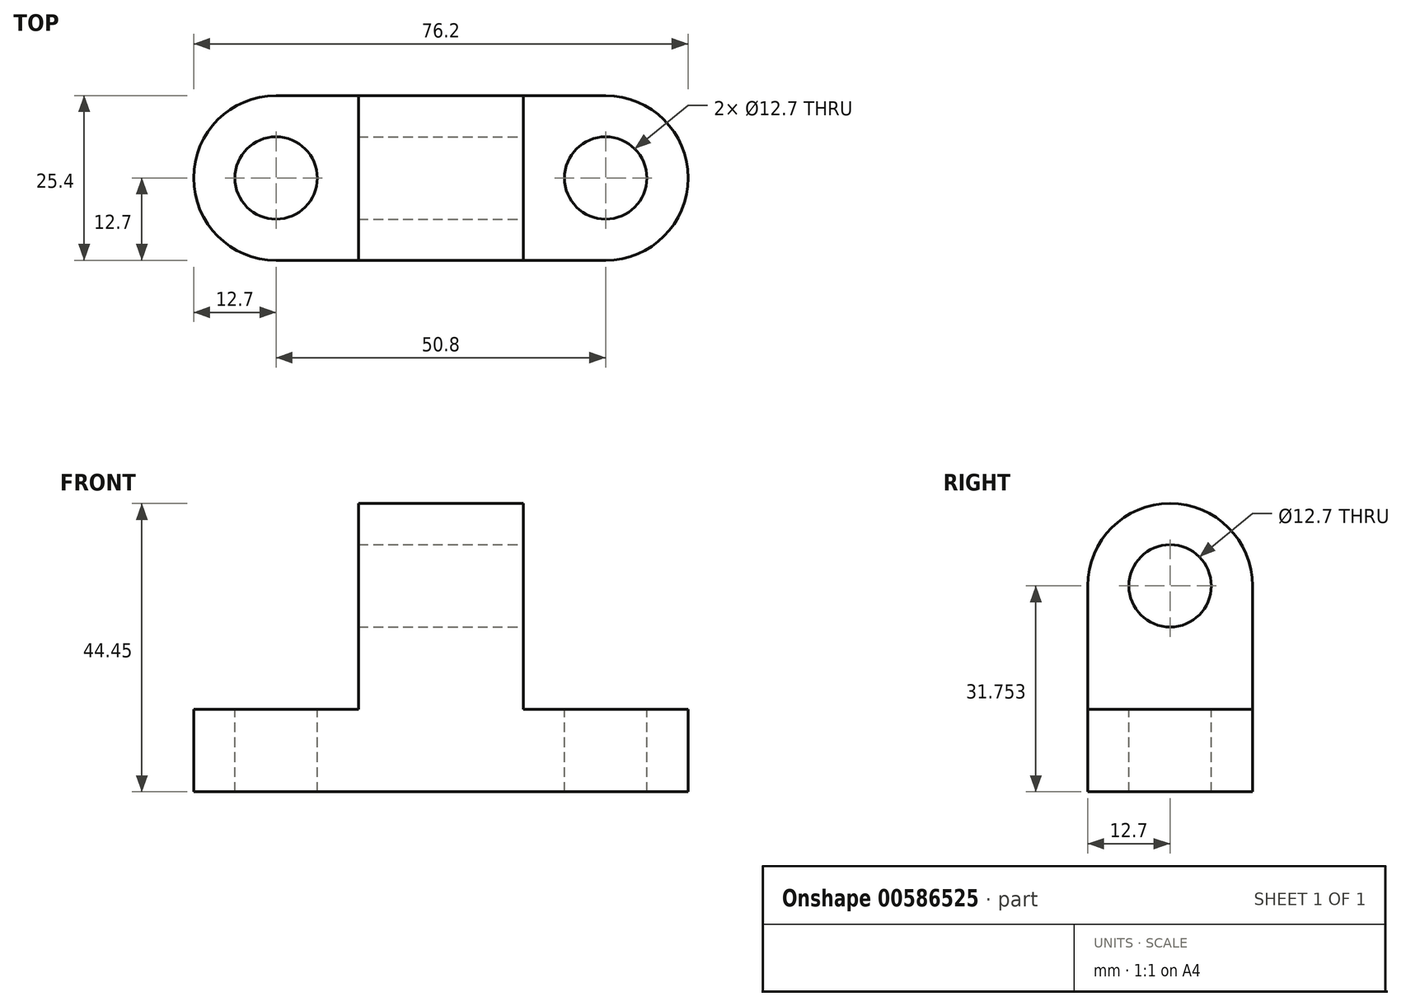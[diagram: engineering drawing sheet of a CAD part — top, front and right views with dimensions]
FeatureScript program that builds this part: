
annotation { "Feature Type Name" : "Feature", "Feature Type Description" : "" }
export const myFeature = defineFeature(function(context is Context, id is Id, definition is map)
    precondition{}
    {
        {
            var Q0;
            Q0=qCreatedBy(makeId("Front.planeOp"),FACE);
            var sketch = newSketch(context, id + "F0", { "sketchPlane" : qUnion([Q0])});
            skLineSegment(sketch, "E0", {"start": v(-85.26, 10.9) * mm, "end": v(-85.26, -1.8) * mm});
            skLineSegment(sketch, "E1", {"start": v(-85.26, -1.8) * mm, "end": v(-9.06, -1.8) * mm});
            skLineSegment(sketch, "E2", {"start": v(-9.06, -1.8) * mm, "end": v(-9.06, 10.9) * mm});
            skLineSegment(sketch, "E3", {"start": v(-9.06, 10.9) * mm, "end": v(-34.46, 10.9) * mm});
            skLineSegment(sketch, "E4", {"start": v(-34.46, 10.9) * mm, "end": v(-34.46, 42.65) * mm});
            skLineSegment(sketch, "E5", {"start": v(-34.46, 42.65) * mm, "end": v(-59.86, 42.65) * mm});
            skLineSegment(sketch, "E6", {"start": v(-59.86, 42.65) * mm, "end": v(-59.86, 10.9) * mm});
            skLineSegment(sketch, "E7", {"start": v(-59.86, 10.9) * mm, "end": v(-85.26, 10.9) * mm});
            skSolve(sketch);
        }
        {
            var Q0;
            Q0 = qSketchRegion(id + "F0", true);
            extrude(context, id + "F1", {"entities" : qUnion([Q0]), "depth" : 25.4 * mm, "offsetDistance" : 25.4 * mm});
        }
        {
            var Q0;
            Q0=makeQuery(id+"F1.opExtrude","SWEPT_FACE",FACE,{"disambiguationData":[OSD([sQuery(id+"F0.wireOp",EDGE,"E4")])]});
            var sketch = newSketch(context, id + "F2", { "sketchPlane" : qUnion([Q0])});
            skArc(sketch, "E8", {"start": v(0, 29.95) * mm, "mid": v(-12.7, 42.65) * mm, "end": v(-25.4, 29.95) * mm});
            skCircle(sketch, "E9", {"center": v(-12.7, 29.95) * mm, "radius": 6.35 * mm});
            skSolve(sketch);
        }
        {
            var Q0;
            Q0 = qSketchRegion(id + "F2", true);
            var Q1;
            {var subQ0=sQuery(id+"F2.wireOp",EDGE,"E8");var subQ1=sQuery(id+"F0.wireOp",EDGE,"E4");var subQ2=makeQuery(id+"F1.opExtrude","CAP_EDGE",EDGE,{"disambiguationData":[OSD([subQ1])],"isStart":true});var subQ3=makeQuery(id+"F2.imprint","INTERSECT",VERTEX,{"derivedFrom":[subQ2,subQ0]});Q1=makeQuery(id+"F2.imprint","IMPRINT",FACE,{"disambiguationData":[TD([[makeQuery(id+"F2.imprint","IMPRINT",EDGE,{"disambiguationData":[TD([[subQ3,-1.0]])],"derivedFrom":subQ0}),-1.0]])]});}
            var Q2;
            {var subQ0=sQuery(id+"F2.wireOp",EDGE,"E8");var subQ1=sQuery(id+"F0.wireOp",EDGE,"E4");var subQ2=makeQuery(id+"F1.opExtrude","CAP_EDGE",EDGE,{"disambiguationData":[OSD([subQ1])],"isStart":false});var subQ3=makeQuery(id+"F2.imprint","INTERSECT",VERTEX,{"derivedFrom":[subQ2,subQ0]});Q2=makeQuery(id+"F2.imprint","IMPRINT",FACE,{"disambiguationData":[TD([[makeQuery(id+"F2.imprint","IMPRINT",EDGE,{"disambiguationData":[TD([[subQ3,1.0]])],"derivedFrom":subQ0}),-1.0]])]});}
            extrude(context, id + "F3", {"entities" : qUnion([Q0, Q1, Q2]), "operationType" : NewBodyOperationType.REMOVE, "oppositeDirection" : true, "depth" : 25.4 * mm, "offsetDistance" : 25.4 * mm});
        }
        {
            var Q0;
            Q0=makeQuery(id+"F1.opExtrude","SWEPT_FACE",FACE,{"disambiguationData":[OSD([sQuery(id+"F0.wireOp",EDGE,"E3")])]});
            var sketch = newSketch(context, id + "F4", { "sketchPlane" : qUnion([Q0])});
            skArc(sketch, "E10", {"start": v(-21.76, -25.4) * mm, "mid": v(-9.06, -12.7) * mm, "end": v(-21.76, 0) * mm});
            skCircle(sketch, "E11", {"center": v(-21.76, -12.7) * mm, "radius": 6.35 * mm});
            skSolve(sketch);
        }
        {
            var Q0;
            Q0 = qSketchRegion(id + "F4", true);
            var Q1;
            {var subQ0=sQuery(id+"F4.wireOp",EDGE,"E10");var subQ1=sQuery(id+"F0.wireOp",EDGE,"E3");var subQ2=makeQuery(id+"F1.opExtrude","CAP_EDGE",EDGE,{"disambiguationData":[OSD([subQ1])],"isStart":true});var subQ3=makeQuery(id+"F4.imprint","INTERSECT",VERTEX,{"derivedFrom":[subQ2,subQ0]});Q1=makeQuery(id+"F4.imprint","IMPRINT",FACE,{"disambiguationData":[TD([[makeQuery(id+"F4.imprint","IMPRINT",EDGE,{"disambiguationData":[TD([[subQ3,1.0]])],"derivedFrom":subQ0}),-1.0]])]});}
            var Q2;
            {var subQ0=sQuery(id+"F4.wireOp",EDGE,"E10");var subQ1=sQuery(id+"F0.wireOp",EDGE,"E3");var subQ2=makeQuery(id+"F1.opExtrude","CAP_EDGE",EDGE,{"disambiguationData":[OSD([subQ1])],"isStart":false});var subQ3=makeQuery(id+"F4.imprint","INTERSECT",VERTEX,{"derivedFrom":[subQ2,subQ0]});Q2=makeQuery(id+"F4.imprint","IMPRINT",FACE,{"disambiguationData":[TD([[makeQuery(id+"F4.imprint","IMPRINT",EDGE,{"disambiguationData":[TD([[subQ3,-1.0]])],"derivedFrom":subQ0}),-1.0]])]});}
            extrude(context, id + "F5", {"entities" : qUnion([Q0, Q1, Q2]), "operationType" : NewBodyOperationType.REMOVE, "oppositeDirection" : true, "depth" : 25.4 * mm, "offsetDistance" : 25.4 * mm});
        }
        {
            var Q0;
            Q0=makeQuery(id+"F1.opExtrude","SWEPT_FACE",FACE,{"disambiguationData":[OSD([sQuery(id+"F0.wireOp",EDGE,"E7")])]});
            var sketch = newSketch(context, id + "F6", { "sketchPlane" : qUnion([Q0])});
            skArc(sketch, "E12", {"start": v(-72.56, 0) * mm, "mid": v(-85.26, -12.7) * mm, "end": v(-72.56, -25.4) * mm});
            skCircle(sketch, "E13", {"center": v(-72.56, -12.7) * mm, "radius": 6.35 * mm});
            skSolve(sketch);
        }
        {
            var Q0;
            Q0 = qSketchRegion(id + "F6", true);
            var Q1;
            {var subQ0=sQuery(id+"F6.wireOp",EDGE,"E12");var subQ1=sQuery(id+"F0.wireOp",EDGE,"E7");var subQ2=makeQuery(id+"F1.opExtrude","CAP_EDGE",EDGE,{"disambiguationData":[OSD([subQ1])],"isStart":true});var subQ3=makeQuery(id+"F6.imprint","INTERSECT",VERTEX,{"derivedFrom":[subQ2,subQ0]});Q1=makeQuery(id+"F6.imprint","IMPRINT",FACE,{"disambiguationData":[TD([[makeQuery(id+"F6.imprint","IMPRINT",EDGE,{"disambiguationData":[TD([[subQ3,-1.0]])],"derivedFrom":subQ0}),-1.0]])]});}
            var Q2;
            {var subQ0=sQuery(id+"F6.wireOp",EDGE,"E12");var subQ1=sQuery(id+"F0.wireOp",EDGE,"E7");var subQ2=makeQuery(id+"F1.opExtrude","CAP_EDGE",EDGE,{"disambiguationData":[OSD([subQ1])],"isStart":false});var subQ3=makeQuery(id+"F6.imprint","INTERSECT",VERTEX,{"derivedFrom":[subQ2,subQ0]});Q2=makeQuery(id+"F6.imprint","IMPRINT",FACE,{"disambiguationData":[TD([[makeQuery(id+"F6.imprint","IMPRINT",EDGE,{"disambiguationData":[TD([[subQ3,1.0]])],"derivedFrom":subQ0}),-1.0]])]});}
            extrude(context, id + "F7", {"entities" : qUnion([Q0, Q1, Q2]), "operationType" : NewBodyOperationType.REMOVE, "oppositeDirection" : true, "depth" : 25.4 * mm, "offsetDistance" : 25.4 * mm});
        }
    });
